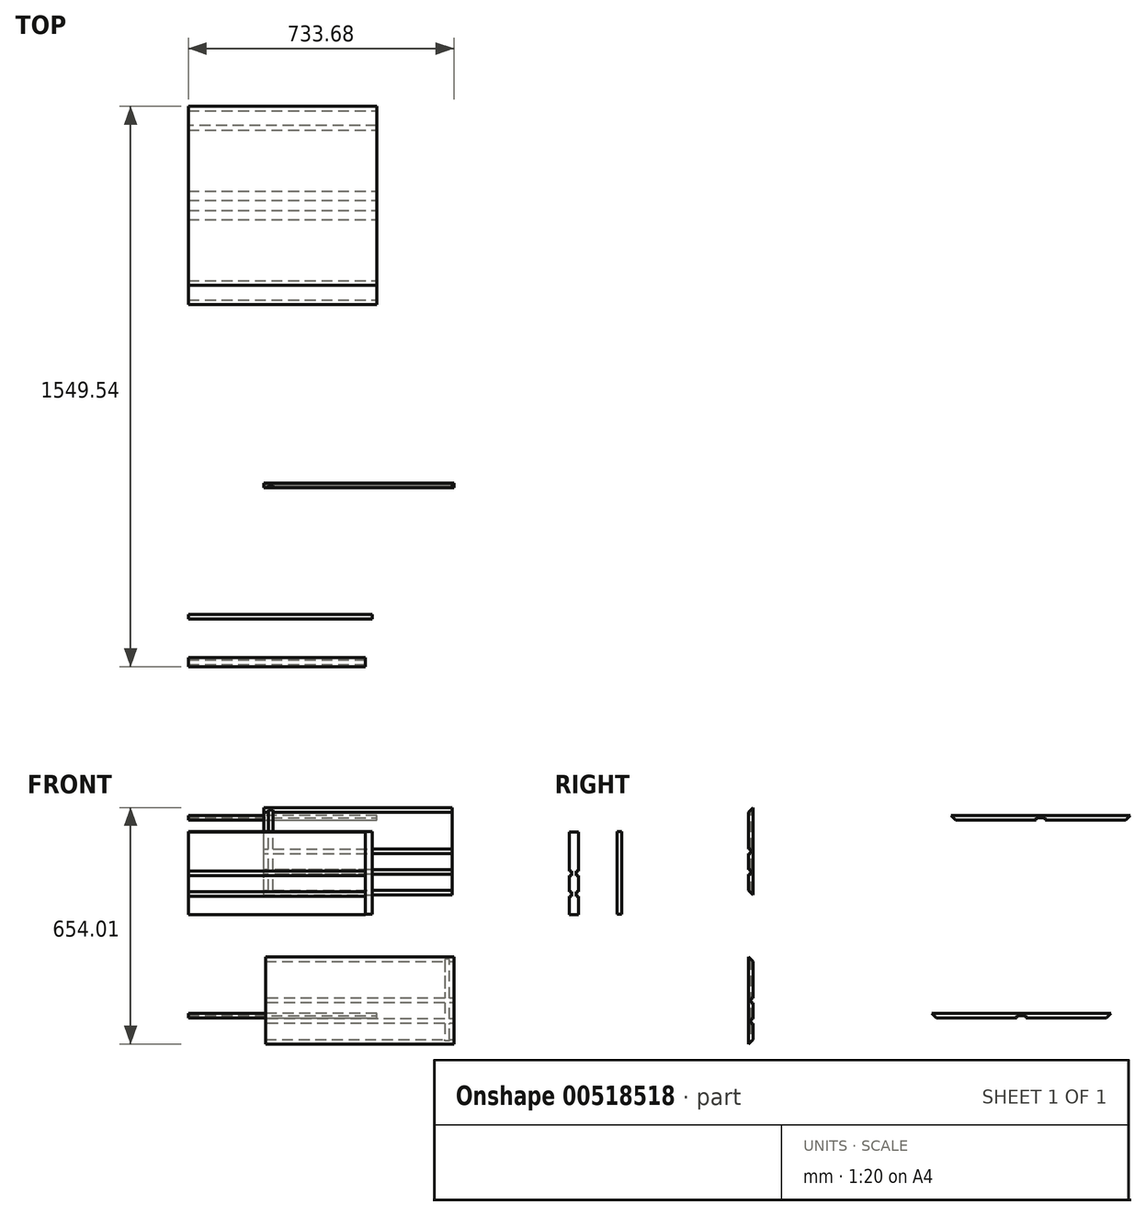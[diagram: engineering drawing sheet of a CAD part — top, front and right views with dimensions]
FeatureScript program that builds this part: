
annotation { "Feature Type Name" : "Feature", "Feature Type Description" : "" }
export const myFeature = defineFeature(function(context is Context, id is Id, definition is map)
    precondition{}
    {
        {
            var Q0;
            Q0=qCreatedBy(makeId("Front.planeOp"),FACE);
            var sketch = newSketch(context, id + "F0", { "sketchPlane" : qUnion([Q0])});
            skLineSegment(sketch, "E0", {"start": v(208.9, 23.55) * mm, "end": v(208.9, 264.85) * mm});
            skLineSegment(sketch, "E1", {"start": v(208.9, 264.85) * mm, "end": v(729.6, 264.85) * mm});
            skLineSegment(sketch, "E2", {"start": v(729.6, 264.85) * mm, "end": v(729.6, 23.55) * mm});
            skLineSegment(sketch, "E3", {"start": v(208.9, 23.55) * mm, "end": v(729.6, 23.55) * mm});
            skPoint(sketch, "E4.orphan", {"position": v(729.6, 0) * mm});
            skSolve(sketch);
        }
        {
            var Q0;
            Q0=makeQuery(id+"F0.imprint","IMPRINT",FACE,{"disambiguationData":[TD([[makeQuery(id+"F0.imprint","IMPRINT",EDGE,{"derivedFrom":sQuery(id+"F0.wireOp",EDGE,"E0")}),-1.0]])]});
            extrude(context, id + "F1", {"entities" : qUnion([Q0]), "depth" : 12.7 * mm, "offsetDistance" : 25.4 * mm});
        }
        {
            var Q0;
            Q0=makeQuery(id+"F1.opExtrude","SWEPT_FACE",FACE,{"disambiguationData":[OSD([sQuery(id+"F0.wireOp",EDGE,"E2")])]});
            var sketch = newSketch(context, id + "F2", { "sketchPlane" : qUnion([Q0])});
            skLineSegment(sketch, "E5", {"start": v(-12.7, 252.15) * mm, "end": v(0, 264.85) * mm});
            skLineSegment(sketch, "E6", {"start": v(-12.7, 264.85) * mm, "end": v(-12.7, 252.15) * mm});
            skLineSegment(sketch, "E7", {"start": v(-12.7, 36.25) * mm, "end": v(0, 23.55) * mm});
            skLineSegment(sketch, "E8", {"start": v(-12.7, 36.25) * mm, "end": v(-12.7, 23.55) * mm});
            skLineSegment(sketch, "E9", {"start": v(-12.7, 23.55) * mm, "end": v(0, 23.55) * mm});
            skSolve(sketch);
        }
        {
            var Q0;
            Q0=makeQuery(id+"F2.imprint","IMPRINT",FACE,{"disambiguationData":[TD([[makeQuery(id+"F2.imprint","IMPRINT",EDGE,{"derivedFrom":sQuery(id+"F2.wireOp",EDGE,"E7")}),-1.0]])]});
            var Q1;
            Q1=makeQuery(id+"F2.imprint","IMPRINT",FACE,{"disambiguationData":[TD([[makeQuery(id+"F2.imprint","IMPRINT",EDGE,{"derivedFrom":sQuery(id+"F2.wireOp",EDGE,"E5")}),1.0]])]});
            extrude(context, id + "F3", {"entities" : qUnion([Q0, Q1]), "operationType" : NewBodyOperationType.REMOVE, "endBound" : BoundingType.THROUGH_ALL, "oppositeDirection" : true, "depth" : 25.4 * mm, "offsetDistance" : 25.4 * mm});
        }
        {
            var Q0;
            Q0=makeQuery(id+"F1.opExtrude","CAP_FACE",FACE,{"disambiguationData":[OSD([sQuery(id+"F0.wireOp",EDGE,"E0"),sQuery(id+"F0.wireOp",EDGE,"E1"),sQuery(id+"F0.wireOp",EDGE,"E2"),sQuery(id+"F0.wireOp",EDGE,"E3")])],"isStart":false});
            var sketch = newSketch(context, id + "F4", { "sketchPlane" : qUnion([Q0])});
            skLineSegment(sketch, "E10.0", {"start": v(208.9, 137.85) * mm, "end": v(729.6, 137.85) * mm});
            skLineSegment(sketch, "E11.0", {"start": v(208.9, 150.55) * mm, "end": v(729.6, 150.55) * mm});
            skPoint(sketch, "E12.end.orphan", {"position": v(729.6, 144.2) * mm});
            skPoint(sketch, "E12.start.orphan", {"position": v(208.9, 144.2) * mm});
            skLineSegment(sketch, "E13", {"start": v(208.9, 150.55) * mm, "end": v(208.9, 137.85) * mm});
            skLineSegment(sketch, "E14", {"start": v(729.6, 150.55) * mm, "end": v(729.6, 137.85) * mm});
            skSolve(sketch);
        }
        {
            var Q0;
            Q0=makeQuery(id+"F4.imprint","IMPRINT",FACE,{"disambiguationData":[TD([[makeQuery(id+"F4.imprint","IMPRINT",EDGE,{"derivedFrom":sQuery(id+"F4.wireOp",EDGE,"E10.0")}),1.0]])]});
            extrude(context, id + "F5", {"entities" : qUnion([Q0]), "operationType" : NewBodyOperationType.REMOVE, "oppositeDirection" : true, "depth" : 6.35 * mm, "offsetDistance" : 25.4 * mm});
        }
        {
            var Q0;
            {var subQ0=sQuery(id+"F0.wireOp",EDGE,"E0");var subQ1=sQuery(id+"F0.wireOp",EDGE,"E2");Q0=makeQuery(id+"F5.boolean.opBoolean","SPLIT",FACE,{"disambiguationData":[TD([makeQuery(id+"F3.boolean.opBoolean","COPY",FACE,{"derivedFrom":makeQuery(id+"F3.opExtrude","SWEPT_FACE",FACE,{"disambiguationData":[OSD([sQuery(id+"F2.wireOp",EDGE,"E7")])]})})])],"derivedFrom":makeQuery(id+"F1.opExtrude","CAP_FACE",FACE,{"disambiguationData":[OSD([subQ0,sQuery(id+"F0.wireOp",EDGE,"E1"),subQ1,sQuery(id+"F0.wireOp",EDGE,"E3")])],"isStart":false})});}
            var sketch = newSketch(context, id + "F6", { "sketchPlane" : qUnion([Q0])});
            skLineSegment(sketch, "E15", {"start": v(208.9, 137.85) * mm, "end": v(221.6, 137.85) * mm});
            skLineSegment(sketch, "E16", {"start": v(221.6, 137.85) * mm, "end": v(221.6, 270.98) * mm});
            skLineSegment(sketch, "E17", {"start": v(221.6, 137.85) * mm, "end": v(221.6, 8.17) * mm});
            skLineSegment(sketch, "E18", {"start": v(221.6, 8.17) * mm, "end": v(234.3, 8.17) * mm});
            skLineSegment(sketch, "E19", {"start": v(234.3, 8.17) * mm, "end": v(234.3, 264.9) * mm});
            skLineSegment(sketch, "E20", {"start": v(234.3, 264.9) * mm, "end": v(221.6, 270.98) * mm});
            skSolve(sketch);
        }
        {
            var Q0;
            Q0 = qSketchRegion(id + "F6", true);
            extrude(context, id + "F7", {"entities" : qUnion([Q0]), "operationType" : NewBodyOperationType.REMOVE, "oppositeDirection" : true, "depth" : 6.35 * mm, "offsetDistance" : 25.4 * mm});
        }
        {
            var Q0;
            Q0=qCreatedBy(makeId("Front.planeOp"),FACE);
            var sketch = newSketch(context, id + "F8", { "sketchPlane" : qUnion([Q0])});
            skLineSegment(sketch, "E21", {"start": v(212.98, -147.86) * mm, "end": v(733.68, -147.86) * mm});
            skLineSegment(sketch, "E22", {"start": v(733.68, -147.86) * mm, "end": v(733.68, -389.16) * mm});
            skLineSegment(sketch, "E23", {"start": v(733.68, -389.16) * mm, "end": v(212.98, -389.16) * mm});
            skLineSegment(sketch, "E24", {"start": v(212.98, -389.16) * mm, "end": v(212.98, -147.86) * mm});
            skSolve(sketch);
        }
        {
            var Q0;
            Q0 = qSketchRegion(id + "F8", true);
            extrude(context, id + "F9", {"entities" : qUnion([Q0]), "depth" : 12.7 * mm, "offsetDistance" : 25.4 * mm});
        }
        {
            var Q0;
            Q0=makeQuery(id+"F9.opExtrude","SWEPT_FACE",FACE,{"disambiguationData":[OSD([sQuery(id+"F8.wireOp",EDGE,"E22")])]});
            var sketch = newSketch(context, id + "F10", { "sketchPlane" : qUnion([Q0])});
            skLineSegment(sketch, "E25", {"start": v(0, -160.56) * mm, "end": v(0, -147.86) * mm});
            skLineSegment(sketch, "E26", {"start": v(0, -147.86) * mm, "end": v(-12.7, -147.86) * mm});
            skLineSegment(sketch, "E27", {"start": v(0, -160.56) * mm, "end": v(-12.7, -147.86) * mm});
            skLineSegment(sketch, "E28", {"start": v(0, -376.46) * mm, "end": v(-12.7, -389.16) * mm});
            skLineSegment(sketch, "E29", {"start": v(0, -376.46) * mm, "end": v(0, -389.16) * mm});
            skLineSegment(sketch, "E30", {"start": v(0, -389.16) * mm, "end": v(-12.7, -389.16) * mm});
            skSolve(sketch);
        }
        {
            var Q0;
            Q0 = qSketchRegion(id + "F10", true);
            extrude(context, id + "F11", {"entities" : qUnion([Q0]), "operationType" : NewBodyOperationType.REMOVE, "endBound" : BoundingType.THROUGH_ALL, "oppositeDirection" : true, "depth" : 25.4 * mm, "offsetDistance" : 25.4 * mm});
        }
        {
            var Q0;
            Q0=makeQuery(id+"F9.opExtrude","CAP_FACE",FACE,{"disambiguationData":[OSD([sQuery(id+"F8.wireOp",EDGE,"E21"),sQuery(id+"F8.wireOp",EDGE,"E22"),sQuery(id+"F8.wireOp",EDGE,"E23"),sQuery(id+"F8.wireOp",EDGE,"E24")])],"isStart":true});
            var sketch = newSketch(context, id + "F12", { "sketchPlane" : qUnion([Q0])});
            skLineSegment(sketch, "E31.0", {"start": v(-733.68, -274.86) * mm, "end": v(-212.98, -274.86) * mm});
            skLineSegment(sketch, "E32.0", {"start": v(-733.68, -262.16) * mm, "end": v(-212.98, -262.16) * mm});
            skLineSegment(sketch, "E33", {"start": v(-733.68, -262.16) * mm, "end": v(-733.68, -274.86) * mm});
            skLineSegment(sketch, "E34", {"start": v(-212.98, -262.16) * mm, "end": v(-212.98, -274.86) * mm});
            skSolve(sketch);
        }
        {
            var Q0;
            Q0=makeQuery(id+"F12.imprint","IMPRINT",FACE,{"disambiguationData":[TD([[makeQuery(id+"F12.imprint","IMPRINT",EDGE,{"derivedFrom":sQuery(id+"F12.wireOp",EDGE,"E31.0")}),1.0]])]});
            extrude(context, id + "F13", {"entities" : qUnion([Q0]), "operationType" : NewBodyOperationType.REMOVE, "oppositeDirection" : true, "depth" : 6.35 * mm, "offsetDistance" : 25.4 * mm});
        }
        {
            var Q0;
            {var subQ0=sQuery(id+"F8.wireOp",EDGE,"E22");var subQ1=sQuery(id+"F8.wireOp",EDGE,"E24");Q0=makeQuery(id+"F13.boolean.opBoolean","SPLIT",FACE,{"disambiguationData":[TD([makeQuery(id+"F11.boolean.opBoolean","COPY",FACE,{"derivedFrom":makeQuery(id+"F11.opExtrude","SWEPT_FACE",FACE,{"disambiguationData":[OSD([sQuery(id+"F10.wireOp",EDGE,"E27")])]})})])],"derivedFrom":makeQuery(id+"F9.opExtrude","CAP_FACE",FACE,{"disambiguationData":[OSD([sQuery(id+"F8.wireOp",EDGE,"E21"),subQ0,sQuery(id+"F8.wireOp",EDGE,"E23"),subQ1])],"isStart":true})});}
            var sketch = newSketch(context, id + "F14", { "sketchPlane" : qUnion([Q0])});
            skLineSegment(sketch, "E35", {"start": v(-733.68, -262.16) * mm, "end": v(-720.98, -262.16) * mm});
            skLineSegment(sketch, "E36", {"start": v(-720.98, -262.16) * mm, "end": v(-720.98, -249.46) * mm});
            skLineSegment(sketch, "E37", {"start": v(-720.98, -249.46) * mm, "end": v(-720.98, -127.3) * mm});
            skLineSegment(sketch, "E38", {"start": v(-720.98, -127.3) * mm, "end": v(-708.28, -127.3) * mm});
            skLineSegment(sketch, "E39", {"start": v(-708.28, -127.3) * mm, "end": v(-708.28, -380.86) * mm});
            skLineSegment(sketch, "E40", {"start": v(-708.28, -380.86) * mm, "end": v(-720.98, -380.86) * mm});
            skLineSegment(sketch, "E41", {"start": v(-720.98, -380.86) * mm, "end": v(-720.98, -262.16) * mm});
            skSolve(sketch);
        }
        {
            var Q0;
            Q0 = qSketchRegion(id + "F14", true);
            extrude(context, id + "F15", {"entities" : qUnion([Q0]), "operationType" : NewBodyOperationType.REMOVE, "oppositeDirection" : true, "depth" : 6.35 * mm, "offsetDistance" : 25.4 * mm});
        }
        {
            var Q0;
            {var subQ0=sQuery(id+"F8.wireOp",EDGE,"E22");var subQ1=makeQuery(id+"F9.opExtrude","SWEPT_FACE",FACE,{"disambiguationData":[OSD([subQ0])]});var subQ3=makeQuery(id+"F11.boolean.opBoolean","COPY",FACE,{"derivedFrom":makeQuery(id+"F11.opExtrude","SWEPT_FACE",FACE,{"disambiguationData":[OSD([sQuery(id+"F10.wireOp",EDGE,"E28")])]})});var subQ4=sQuery(id+"F8.wireOp",EDGE,"E24");Q0=makeQuery(id+"F15.boolean.opBoolean","SPLIT",FACE,{"disambiguationData":[TD([subQ1])],"derivedFrom":makeQuery(id+"F13.boolean.opBoolean","SPLIT",FACE,{"disambiguationData":[TD([subQ3])],"derivedFrom":makeQuery(id+"F9.opExtrude","CAP_FACE",FACE,{"disambiguationData":[OSD([sQuery(id+"F8.wireOp",EDGE,"E21"),subQ0,sQuery(id+"F8.wireOp",EDGE,"E23"),subQ4])],"isStart":true})})});}
            var sketch = newSketch(context, id + "F16", { "sketchPlane" : qUnion([Q0])});
            skPoint(sketch, "E42.endSnap0", {"position": v(-733.68, -325.66) * mm});
            skLineSegment(sketch, "E43.0", {"start": v(-733.68, -332.01) * mm, "end": v(-212.98, -332.01) * mm});
            skLineSegment(sketch, "E44.0", {"start": v(-733.68, -319.31) * mm, "end": v(-212.98, -319.31) * mm});
            skLineSegment(sketch, "E45", {"start": v(-733.68, -319.31) * mm, "end": v(-733.68, -332.01) * mm});
            skLineSegment(sketch, "E46", {"start": v(-212.98, -319.31) * mm, "end": v(-212.98, -332.01) * mm});
            skSolve(sketch);
        }
        {
            var Q0;
            Q0 = qSketchRegion(id + "F16", true);
            extrude(context, id + "F17", {"entities" : qUnion([Q0]), "operationType" : NewBodyOperationType.REMOVE, "oppositeDirection" : true, "depth" : 6.35 * mm, "offsetDistance" : 25.4 * mm});
        }
        {
            var Q0;
            {var subQ0=sQuery(id+"F0.wireOp",EDGE,"E2");var subQ1=makeQuery(id+"F1.opExtrude","SWEPT_FACE",FACE,{"disambiguationData":[OSD([subQ0])]});var subQ2=makeQuery(id+"F3.boolean.opBoolean","COPY",FACE,{"derivedFrom":makeQuery(id+"F3.opExtrude","SWEPT_FACE",FACE,{"disambiguationData":[OSD([sQuery(id+"F2.wireOp",EDGE,"E7")])]})});var subQ4=sQuery(id+"F0.wireOp",EDGE,"E0");Q0=makeQuery(id+"F7.boolean.opBoolean","SPLIT",FACE,{"disambiguationData":[TD([subQ1])],"derivedFrom":makeQuery(id+"F5.boolean.opBoolean","SPLIT",FACE,{"disambiguationData":[TD([subQ2])],"derivedFrom":makeQuery(id+"F1.opExtrude","CAP_FACE",FACE,{"disambiguationData":[OSD([subQ4,sQuery(id+"F0.wireOp",EDGE,"E1"),subQ0,sQuery(id+"F0.wireOp",EDGE,"E3")])],"isStart":false})})});}
            var sketch = newSketch(context, id + "F18", { "sketchPlane" : qUnion([Q0])});
            skPoint(sketch, "E47.endSnap0", {"position": v(234.3, 87.05) * mm});
            skLineSegment(sketch, "E48.0", {"start": v(729.6, 93.4) * mm, "end": v(199.62, 93.4) * mm});
            skLineSegment(sketch, "E49.0", {"start": v(729.6, 80.7) * mm, "end": v(199.62, 80.7) * mm});
            skLineSegment(sketch, "E50", {"start": v(199.62, 93.4) * mm, "end": v(199.62, 80.7) * mm});
            skLineSegment(sketch, "E51", {"start": v(729.6, 93.4) * mm, "end": v(729.6, 80.7) * mm});
            skSolve(sketch);
        }
        {
            var Q0;
            Q0 = qSketchRegion(id + "F18", true);
            extrude(context, id + "F19", {"entities" : qUnion([Q0]), "operationType" : NewBodyOperationType.REMOVE, "oppositeDirection" : true, "depth" : 6.35 * mm, "offsetDistance" : 25.4 * mm});
        }
        {
            var Q0;
            Q0=qCreatedBy(makeId("Right.planeOp"),FACE);
            var sketch = newSketch(context, id + "F20", { "sketchPlane" : qUnion([Q0])});
            skLineSegment(sketch, "E52", {"start": v(-507.14, -31.45) * mm, "end": v(-481.74, -31.45) * mm});
            skLineSegment(sketch, "E53", {"start": v(-481.74, -31.45) * mm, "end": v(-481.74, 197.15) * mm});
            skLineSegment(sketch, "E54", {"start": v(-481.74, 197.15) * mm, "end": v(-507.14, 197.15) * mm});
            skLineSegment(sketch, "E55", {"start": v(-507.14, 197.15) * mm, "end": v(-507.14, -31.45) * mm});
            skSolve(sketch);
        }
        {
            var Q0;
            Q0 = qSketchRegion(id + "F20", true);
            extrude(context, id + "F21", {"entities" : qUnion([Q0]), "depth" : 488.95 * mm, "offsetDistance" : 25.4 * mm});
        }
        {
            var Q0;
            Q0=makeQuery(id+"F21.opExtrude","SWEPT_FACE",FACE,{"disambiguationData":[OSD([sQuery(id+"F20.wireOp",EDGE,"E55")])]});
            var sketch = newSketch(context, id + "F22", { "sketchPlane" : qUnion([Q0])});
            skLineSegment(sketch, "E56.0", {"start": v(0, 76.5) * mm, "end": v(488.95, 76.5) * mm});
            skLineSegment(sketch, "E57.0", {"start": v(0, 89.2) * mm, "end": v(488.95, 89.2) * mm});
            skLineSegment(sketch, "E58", {"start": v(0, 89.2) * mm, "end": v(0, 76.5) * mm});
            skLineSegment(sketch, "E59", {"start": v(488.95, 89.2) * mm, "end": v(488.95, 76.5) * mm});
            skSolve(sketch);
        }
        {
            var Q0;
            Q0=makeQuery(id+"F22.imprint","IMPRINT",FACE,{"disambiguationData":[TD([[makeQuery(id+"F22.imprint","IMPRINT",EDGE,{"derivedFrom":sQuery(id+"F22.wireOp",EDGE,"E56.0")}),1.0]])]});
            extrude(context, id + "F23", {"entities" : qUnion([Q0]), "operationType" : NewBodyOperationType.REMOVE, "oppositeDirection" : true, "depth" : 6.35 * mm, "offsetDistance" : 25.4 * mm});
        }
        {
            var Q0;
            Q0=makeQuery(id+"F21.opExtrude","CAP_FACE",FACE,{"disambiguationData":[OSD([sQuery(id+"F20.wireOp",EDGE,"E52"),sQuery(id+"F20.wireOp",EDGE,"E53"),sQuery(id+"F20.wireOp",EDGE,"E54"),sQuery(id+"F20.wireOp",EDGE,"E55")])],"isStart":false});
            var sketch = newSketch(context, id + "F24", { "sketchPlane" : qUnion([Q0])});
            skPoint(sketch, "E60.endSnap0", {"position": v(-503.97, 89.2) * mm});
            skLineSegment(sketch, "E61", {"start": v(-488.1, 89.2) * mm, "end": v(-488.1, 76.5) * mm});
            skLineSegment(sketch, "E62", {"start": v(-488.1, 76.5) * mm, "end": v(-481.74, 76.5) * mm});
            skPoint(sketch, "E62.endSnap0", {"position": v(-503.97, 76.5) * mm});
            skLineSegment(sketch, "E63", {"start": v(-481.74, 76.5) * mm, "end": v(-481.74, 89.2) * mm});
            skLineSegment(sketch, "E64", {"start": v(-481.74, 89.2) * mm, "end": v(-488.1, 89.2) * mm});
            skSolve(sketch);
        }
        {
            var Q0;
            Q0=makeQuery(id+"F24.imprint","IMPRINT",FACE,{"disambiguationData":[TD([[makeQuery(id+"F24.imprint","IMPRINT",EDGE,{"derivedFrom":sQuery(id+"F24.wireOp",EDGE,"E61")}),1.0]])]});
            extrude(context, id + "F25", {"entities" : qUnion([Q0]), "operationType" : NewBodyOperationType.REMOVE, "endBound" : BoundingType.THROUGH_ALL, "oppositeDirection" : true, "depth" : 25.4 * mm, "offsetDistance" : 25.4 * mm});
        }
        {
            var Q0;
            Q0=makeQuery(id+"F21.opExtrude","CAP_FACE",FACE,{"disambiguationData":[OSD([sQuery(id+"F20.wireOp",EDGE,"E52"),sQuery(id+"F20.wireOp",EDGE,"E53"),sQuery(id+"F20.wireOp",EDGE,"E54"),sQuery(id+"F20.wireOp",EDGE,"E55")])],"isStart":false});
            var sketch = newSketch(context, id + "F26", { "sketchPlane" : qUnion([Q0])});
            skLineSegment(sketch, "E65", {"start": v(-481.74, 76.5) * mm, "end": v(-481.74, 32.05) * mm});
            skLineSegment(sketch, "E66", {"start": v(-481.74, 32.05) * mm, "end": v(-507.14, 32.05) * mm});
            skLineSegment(sketch, "E67", {"start": v(-481.74, 32.05) * mm, "end": v(-481.74, 19.35) * mm});
            skLineSegment(sketch, "E68", {"start": v(-481.74, 19.35) * mm, "end": v(-507.14, 19.35) * mm});
            skLineSegment(sketch, "E69", {"start": v(-507.14, 19.35) * mm, "end": v(-507.14, 32.05) * mm});
            skLineSegment(sketch, "E70", {"start": v(-488.1, 76.5) * mm, "end": v(-488.1, 19.35) * mm});
            skLineSegment(sketch, "E71", {"start": v(-500.8, 76.5) * mm, "end": v(-500.8, 19.35) * mm});
            skSolve(sketch);
        }
        {
            var Q0;
            {var subQ0=sQuery(id+"F26.wireOp",EDGE,"E69");Q0=makeQuery(id+"F26.imprint","IMPRINT",FACE,{"disambiguationData":[TD([[makeQuery(id+"F26.imprint","IMPRINT",EDGE,{"derivedFrom":subQ0}),1.0]])]});}
            var Q1;
            {var subQ0=sQuery(id+"F26.wireOp",EDGE,"E67");Q1=makeQuery(id+"F26.imprint","IMPRINT",FACE,{"disambiguationData":[TD([[makeQuery(id+"F26.imprint","IMPRINT",EDGE,{"derivedFrom":subQ0}),1.0]])]});}
            extrude(context, id + "F27", {"entities" : qUnion([Q0, Q1]), "operationType" : NewBodyOperationType.REMOVE, "endBound" : BoundingType.THROUGH_ALL, "oppositeDirection" : true, "depth" : 25.4 * mm, "offsetDistance" : 25.4 * mm});
        }
        {
            var Q0;
            Q0=qCreatedBy(makeId("Right.planeOp"),FACE);
            var sketch = newSketch(context, id + "F28", { "sketchPlane" : qUnion([Q0])});
            skLineSegment(sketch, "E72", {"start": v(547.1, 242.2) * mm, "end": v(1042.4, 242.2) * mm});
            skLineSegment(sketch, "E73", {"start": v(1042.4, 242.2) * mm, "end": v(1042.4, 229.5) * mm});
            skLineSegment(sketch, "E74", {"start": v(1042.4, 229.5) * mm, "end": v(547.1, 229.5) * mm});
            skLineSegment(sketch, "E75", {"start": v(547.1, 229.5) * mm, "end": v(547.1, 242.2) * mm});
            skSolve(sketch);
        }
        {
            var Q0;
            Q0=makeQuery(id+"F28.imprint","IMPRINT",FACE,{"disambiguationData":[TD([[makeQuery(id+"F28.imprint","IMPRINT",EDGE,{"derivedFrom":sQuery(id+"F28.wireOp",EDGE,"E72")}),-1.0]])]});
            extrude(context, id + "F29", {"entities" : qUnion([Q0]), "depth" : 520.7 * mm, "offsetDistance" : 25.4 * mm});
        }
        {
            var Q0;
            Q0=makeQuery(id+"F29.opExtrude","CAP_FACE",FACE,{"disambiguationData":[OSD([sQuery(id+"F28.wireOp",EDGE,"E72"),sQuery(id+"F28.wireOp",EDGE,"E73"),sQuery(id+"F28.wireOp",EDGE,"E74"),sQuery(id+"F28.wireOp",EDGE,"E75")])],"isStart":false});
            var sketch = newSketch(context, id + "F30", { "sketchPlane" : qUnion([Q0])});
            skLineSegment(sketch, "E76", {"start": v(547.1, 242.2) * mm, "end": v(559.8, 242.2) * mm});
            skLineSegment(sketch, "E77", {"start": v(559.8, 242.2) * mm, "end": v(559.8, 229.5) * mm});
            skLineSegment(sketch, "E78", {"start": v(559.8, 229.5) * mm, "end": v(547.1, 242.2) * mm});
            skLineSegment(sketch, "E79", {"start": v(547.1, 242.2) * mm, "end": v(547.1, 229.5) * mm});
            skLineSegment(sketch, "E80", {"start": v(547.1, 229.5) * mm, "end": v(559.8, 229.5) * mm});
            skLineSegment(sketch, "E81", {"start": v(1042.4, 242.2) * mm, "end": v(1029.7, 242.2) * mm});
            skLineSegment(sketch, "E82", {"start": v(1042.4, 229.5) * mm, "end": v(1029.7, 229.5) * mm});
            skLineSegment(sketch, "E83", {"start": v(1029.7, 229.5) * mm, "end": v(1029.7, 242.2) * mm});
            skLineSegment(sketch, "E84", {"start": v(1029.7, 229.5) * mm, "end": v(1042.4, 242.2) * mm});
            skSolve(sketch);
        }
        {
            var Q0;
            Q0=makeQuery(id+"F30.imprint","IMPRINT",FACE,{"disambiguationData":[TD([[makeQuery(id+"F30.imprint","IMPRINT",EDGE,{"derivedFrom":sQuery(id+"F30.wireOp",EDGE,"E78")}),1.0]])]});
            var Q1;
            Q1=makeQuery(id+"F30.imprint","IMPRINT",FACE,{"disambiguationData":[TD([[makeQuery(id+"F30.imprint","IMPRINT",EDGE,{"derivedFrom":sQuery(id+"F30.wireOp",EDGE,"E82")}),-1.0]])]});
            extrude(context, id + "F31", {"entities" : qUnion([Q0, Q1]), "operationType" : NewBodyOperationType.REMOVE, "endBound" : BoundingType.THROUGH_ALL, "oppositeDirection" : true, "depth" : 25.4 * mm, "offsetDistance" : 25.4 * mm});
        }
        {
            var Q0;
            Q0=makeQuery(id+"F29.opExtrude","CAP_FACE",FACE,{"disambiguationData":[OSD([sQuery(id+"F28.wireOp",EDGE,"E72"),sQuery(id+"F28.wireOp",EDGE,"E73"),sQuery(id+"F28.wireOp",EDGE,"E74"),sQuery(id+"F28.wireOp",EDGE,"E75")])],"isStart":false});
            var sketch = newSketch(context, id + "F32", { "sketchPlane" : qUnion([Q0])});
            skLineSegment(sketch, "E85", {"start": v(794.75, 229.5) * mm, "end": v(807.45, 229.5) * mm});
            skLineSegment(sketch, "E86", {"start": v(807.45, 229.5) * mm, "end": v(794.75, 229.5) * mm});
            skLineSegment(sketch, "E87", {"start": v(794.75, 229.5) * mm, "end": v(782.05, 229.5) * mm});
            skLineSegment(sketch, "E88", {"start": v(782.05, 229.5) * mm, "end": v(782.05, 235.85) * mm});
            skLineSegment(sketch, "E89", {"start": v(782.05, 235.85) * mm, "end": v(807.45, 235.85) * mm});
            skLineSegment(sketch, "E90", {"start": v(807.45, 235.85) * mm, "end": v(807.45, 229.5) * mm});
            skSolve(sketch);
        }
        {
            var Q0;
            Q0 = qSketchRegion(id + "F32", true);
            extrude(context, id + "F33", {"entities" : qUnion([Q0]), "operationType" : NewBodyOperationType.REMOVE, "endBound" : BoundingType.THROUGH_ALL, "oppositeDirection" : true, "depth" : 25.4 * mm, "offsetDistance" : 25.4 * mm});
        }
        {
            var Q0;
            Q0=qCreatedBy(makeId("Right.planeOp"),FACE);
            var sketch = newSketch(context, id + "F34", { "sketchPlane" : qUnion([Q0])});
            skLineSegment(sketch, "E91", {"start": v(494.8, -317.53) * mm, "end": v(990.1, -317.53) * mm});
            skLineSegment(sketch, "E92", {"start": v(990.1, -317.53) * mm, "end": v(990.1, -304.83) * mm});
            skLineSegment(sketch, "E93", {"start": v(990.1, -304.83) * mm, "end": v(494.8, -304.83) * mm});
            skLineSegment(sketch, "E94", {"start": v(494.8, -304.83) * mm, "end": v(494.8, -317.53) * mm});
            skSolve(sketch);
        }
        {
            var Q0;
            Q0 = qSketchRegion(id + "F34", true);
            extrude(context, id + "F35", {"entities" : qUnion([Q0]), "depth" : 520.7 * mm, "offsetDistance" : 25.4 * mm});
        }
        {
            var Q0;
            Q0=makeQuery(id+"F35.opExtrude","CAP_FACE",FACE,{"disambiguationData":[OSD([sQuery(id+"F34.wireOp",EDGE,"E91"),sQuery(id+"F34.wireOp",EDGE,"E92"),sQuery(id+"F34.wireOp",EDGE,"E93"),sQuery(id+"F34.wireOp",EDGE,"E94")])],"isStart":false});
            var sketch = newSketch(context, id + "F36", { "sketchPlane" : qUnion([Q0])});
            skLineSegment(sketch, "E95", {"start": v(494.8, -317.53) * mm, "end": v(507.5, -317.53) * mm});
            skLineSegment(sketch, "E96", {"start": v(507.5, -317.53) * mm, "end": v(494.8, -304.83) * mm});
            skLineSegment(sketch, "E97", {"start": v(494.8, -304.83) * mm, "end": v(494.8, -317.53) * mm});
            skLineSegment(sketch, "E98", {"start": v(990.1, -304.83) * mm, "end": v(990.1, -317.53) * mm});
            skLineSegment(sketch, "E99", {"start": v(990.1, -317.53) * mm, "end": v(977.4, -317.53) * mm});
            skLineSegment(sketch, "E100", {"start": v(977.4, -317.53) * mm, "end": v(990.1, -304.83) * mm});
            skSolve(sketch);
        }
        {
            var Q0;
            Q0=makeQuery(id+"F36.imprint","IMPRINT",FACE,{"disambiguationData":[TD([[makeQuery(id+"F36.imprint","IMPRINT",EDGE,{"derivedFrom":sQuery(id+"F36.wireOp",EDGE,"E95")}),1.0]])]});
            var Q1;
            Q1=makeQuery(id+"F36.imprint","IMPRINT",FACE,{"disambiguationData":[TD([[makeQuery(id+"F36.imprint","IMPRINT",EDGE,{"derivedFrom":sQuery(id+"F36.wireOp",EDGE,"E98")}),1.0]])]});
            extrude(context, id + "F37", {"entities" : qUnion([Q0, Q1]), "operationType" : NewBodyOperationType.REMOVE, "endBound" : BoundingType.THROUGH_ALL, "oppositeDirection" : true, "depth" : 25.4 * mm, "offsetDistance" : 25.4 * mm});
        }
        {
            var Q0;
            Q0=makeQuery(id+"F35.opExtrude","CAP_FACE",FACE,{"disambiguationData":[OSD([sQuery(id+"F34.wireOp",EDGE,"E91"),sQuery(id+"F34.wireOp",EDGE,"E92"),sQuery(id+"F34.wireOp",EDGE,"E93"),sQuery(id+"F34.wireOp",EDGE,"E94")])],"isStart":false});
            var sketch = newSketch(context, id + "F38", { "sketchPlane" : qUnion([Q0])});
            skLineSegment(sketch, "E101", {"start": v(742.45, -317.53) * mm, "end": v(755.15, -317.53) * mm});
            skLineSegment(sketch, "E102", {"start": v(755.15, -317.53) * mm, "end": v(755.15, -311.18) * mm});
            skLineSegment(sketch, "E103", {"start": v(742.45, -317.53) * mm, "end": v(729.75, -317.53) * mm});
            skLineSegment(sketch, "E104", {"start": v(729.75, -317.53) * mm, "end": v(729.75, -311.18) * mm});
            skLineSegment(sketch, "E105", {"start": v(729.75, -311.18) * mm, "end": v(755.15, -311.18) * mm});
            skSolve(sketch);
        }
        {
            var Q0;
            Q0 = qSketchRegion(id + "F38", true);
            var Q1;
            Q1=makeQuery(id+"F38.imprint","IMPRINT",FACE,{"disambiguationData":[TD([[makeQuery(id+"F38.imprint","IMPRINT",EDGE,{"derivedFrom":sQuery(id+"F38.wireOp",EDGE,"E101")}),1.0]])]});
            extrude(context, id + "F39", {"entities" : qUnion([Q0, Q1]), "operationType" : NewBodyOperationType.REMOVE, "endBound" : BoundingType.THROUGH_ALL, "oppositeDirection" : true, "depth" : 25.4 * mm, "offsetDistance" : 25.4 * mm});
        }
        {
            var Q0;
            Q0=qCreatedBy(makeId("Right.planeOp"),FACE);
            var sketch = newSketch(context, id + "F40", { "sketchPlane" : qUnion([Q0])});
            skLineSegment(sketch, "E106", {"start": v(-375.18, 198.75) * mm, "end": v(-375.18, -29.85) * mm});
            skLineSegment(sketch, "E107", {"start": v(-375.18, -29.85) * mm, "end": v(-362.48, -29.85) * mm});
            skLineSegment(sketch, "E108", {"start": v(-362.48, -29.85) * mm, "end": v(-362.48, 198.75) * mm});
            skLineSegment(sketch, "E109", {"start": v(-362.48, 198.75) * mm, "end": v(-375.18, 198.75) * mm});
            skSolve(sketch);
        }
        {
            var Q0;
            Q0 = qSketchRegion(id + "F40", true);
            extrude(context, id + "F41", {"entities" : qUnion([Q0]), "depth" : 508 * mm, "offsetDistance" : 25.4 * mm});
        }
    });
